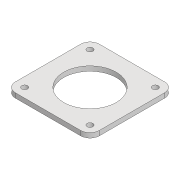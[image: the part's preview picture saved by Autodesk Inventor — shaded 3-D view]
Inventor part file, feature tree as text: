
AUTODESK INVENTOR PART (.ipt)
format: ipt  version: 2020 (Build 240168000, 168)  size: 114,176 bytes
history: native  units: mm
features: mirror x2, other x1, extrude x1, sketch x1
ambient origin geometry x8: Origin, YZ Plane, XZ Plane, XY Plane, X Axis, Y Axis, Z Axis, Center Point
bodies: Body1 (feature_tree)
feature tree (5):
  other  "Sólido1"
  extrude  "Extrusão1"  Depth=36.0mm
  mirror  "Espelhamento1"
  mirror  "Espelhamento2"
  sketch  "Esboço1"  dims[d0=45.0mm d1=36.0mm d2=36.0mm d3=8.0mm d4=5.0mm d5=4.0mm d6=0.0mm d7=8.0mm d8=8.0mm]
